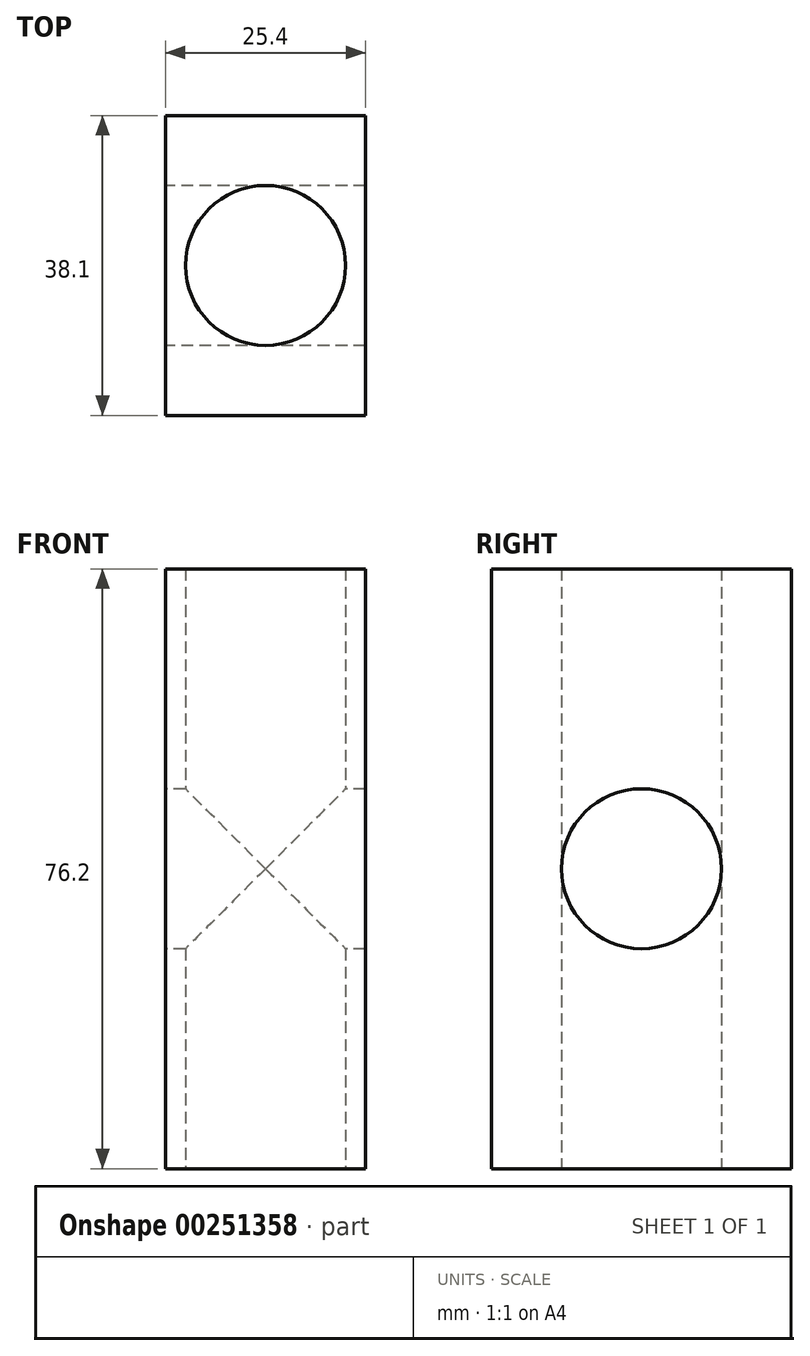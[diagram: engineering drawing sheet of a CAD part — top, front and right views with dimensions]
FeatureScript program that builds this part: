
annotation { "Feature Type Name" : "Feature", "Feature Type Description" : "" }
export const myFeature = defineFeature(function(context is Context, id is Id, definition is map)
    precondition{}
    {
        {
            var Q0;
            Q0=qCreatedBy(makeId("Top.planeOp"),FACE);
            var sketch = newSketch(context, id + "F0", { "sketchPlane" : qUnion([Q0])});
            skLineSegment(sketch, "E0.bottom", {"start": v(0, 0) * mm, "end": v(-25.4, 0) * mm});
            skLineSegment(sketch, "E0.top", {"start": v(0, 38.1) * mm, "end": v(-25.4, 38.1) * mm});
            skLineSegment(sketch, "E0.left", {"start": v(0, 0) * mm, "end": v(0, 38.1) * mm});
            skLineSegment(sketch, "E0.right", {"start": v(-25.4, 0) * mm, "end": v(-25.4, 38.1) * mm});
            skCircle(sketch, "E1", {"center": v(-12.7, 19.05) * mm, "radius": 10.16 * mm});
            skPoint(sketch, "E1.centerSnap0", {"position": v(-12.7, 0) * mm});
            skSolve(sketch);
        }
        {
            var Q0;
            Q0=makeQuery(id+"F0.imprint","IMPRINT",FACE,{"disambiguationData":[TD([[makeQuery(id+"F0.imprint","IMPRINT",EDGE,{"derivedFrom":sQuery(id+"F0.wireOp",EDGE,"E0.bottom")}),-1.0]])]});
            extrude(context, id + "F1", {"entities" : qUnion([Q0]), "depth" : 76.2 * mm});
        }
        {
            var Q0;
            Q0=makeQuery(id+"F1.opExtrude","SWEPT_FACE",FACE,{"disambiguationData":[OSD([sQuery(id+"F0.wireOp",EDGE,"E0.right")])]});
            var sketch = newSketch(context, id + "F2", { "sketchPlane" : qUnion([Q0])});
            skCircle(sketch, "E2", {"center": v(-19.05, 38.1) * mm, "radius": 10.16 * mm});
            skSolve(sketch);
        }
        {
            var Q0;
            Q0=makeQuery(id+"F2.imprint","IMPRINT",FACE,{"disambiguationData":[TD([[makeQuery(id+"F2.imprint","IMPRINT",EDGE,{"derivedFrom":sQuery(id+"F2.wireOp",EDGE,"E2")}),1.0]])]});
            extrude(context, id + "F3", {"entities" : qUnion([Q0]), "operationType" : NewBodyOperationType.REMOVE, "endBound" : BoundingType.THROUGH_ALL, "oppositeDirection" : true, "depth" : 25.4 * mm});
        }
    });
